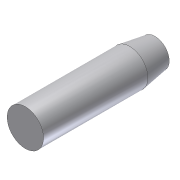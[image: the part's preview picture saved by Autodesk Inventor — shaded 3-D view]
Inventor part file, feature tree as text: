
AUTODESK INVENTOR PART (.ipt)
format: ipt  version: 2012 (Build 160160000, 160)  size: 74,752 bytes
history: native  units: in
note: dims shown in document units (in); Inventor stores cm internally (conversion verified against a paired STEP export)
features: extrude x1, chamfer x1, sketch x1
ambient origin geometry x8: Origin, YZ Plane, XZ Plane, XY Plane, X Axis, Y Axis, Z Axis, Center Point
bodies: Solid1 (feature_tree)
feature tree (3):
  extrude  "Extrusion1"  Depth=5.125in TaperAngle=0.0deg
  chamfer  "Chamfer1"  Distance=0.1562in Angle=45.0deg
  sketch  "Sketch1"  dims[d0=1.4375in d1=5.125in d2=0.0in d3=0.1562in d4=1.0in d5=45.0deg]
